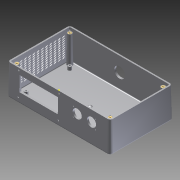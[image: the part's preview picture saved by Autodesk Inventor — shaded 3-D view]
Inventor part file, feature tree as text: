
AUTODESK INVENTOR PART (.ipt)
format: ipt  version: 2015 (Build 190159000, 159)  size: 706,560 bytes
history: native  units: in
note: dims shown in document units (in); Inventor stores cm internally (conversion verified against a paired STEP export)
features: sketch x6, imported_body x5, extrude x4, mirror x3, other x2, rib x1
ambient origin geometry x8: Origin, YZ Plane, XZ Plane, XY Plane, X Axis, Y Axis, Z Axis, Center Point
bodies: Body1 (feature_tree), Body2 (feature_tree), Body3 (feature_tree), Body4 (feature_tree), Body5 (feature_tree)
feature tree (21):
  rib  "Rib2"
  other  "DC-47B_DC-47BPMBY.ipt1"
  sketch  "Sketch1"  dims[d0=0.669in d1=0.669in]
  sketch  "Sketch2"  dims[d2=1.063in d3=0.7874in]
  extrude  "Extrusion2"  Depth=0.669in
  extrude  "Extrusion3"  Depth=0.7874in
  extrude  "Extrusion4"  Depth=0.7874in
  extrude  "Extrusion5"  Depth=0.787in
  other  "_INSERT_-_#4-40 Tapped Hole2_"
  mirror  "Mirror5"
  mirror  "Mirror6[1]"
  mirror  "Mirror6[2]"
  imported_body  "Base1"
  imported_body  "Base2"
  imported_body  "Base3"
  imported_body  "Base4"
  imported_body  "Base5"
  sketch  "Sketch3"  dims[d4=1.1811in d5=0.7874in]
  sketch  "Sketch4"  dims[d27=1.772in d28=0.787in]
  sketch  "Sketch6"  dims[d29=0.354in]
  sketch  "Sketch7"  dims[d30=0.394in d31=0.079in d32=0.0585in d33=0.059in d34=0.059in d35=0.059in d36=0.079in d37=0.0585in d38=0.059in d39=0.079in d40=0.079in d41=0.059in d42=0.059in d43=1.0in d44=0.0in d46=1.0827in d47=2.8543in d48=3.3125in d49=0.0in d59=0.1083in d60=0.0689in d61=0.3839in d62=0.3839in d63=1.7125in d64=1.7125in d65=2.9921in d66=2.815in d67=1.0433in d68=0.0197in d69=0.0197in d90=0.3937in d91=0.3937in d92=0.3937in d93=0.3937in d94=4.7244in d96=0.315in d97=3.937in d99=0.1496in d102=1.0in d103=0.0in d104=0.7874in d105=1.0678in d106=3.6245in d107=1.0in d108=0.0in]
